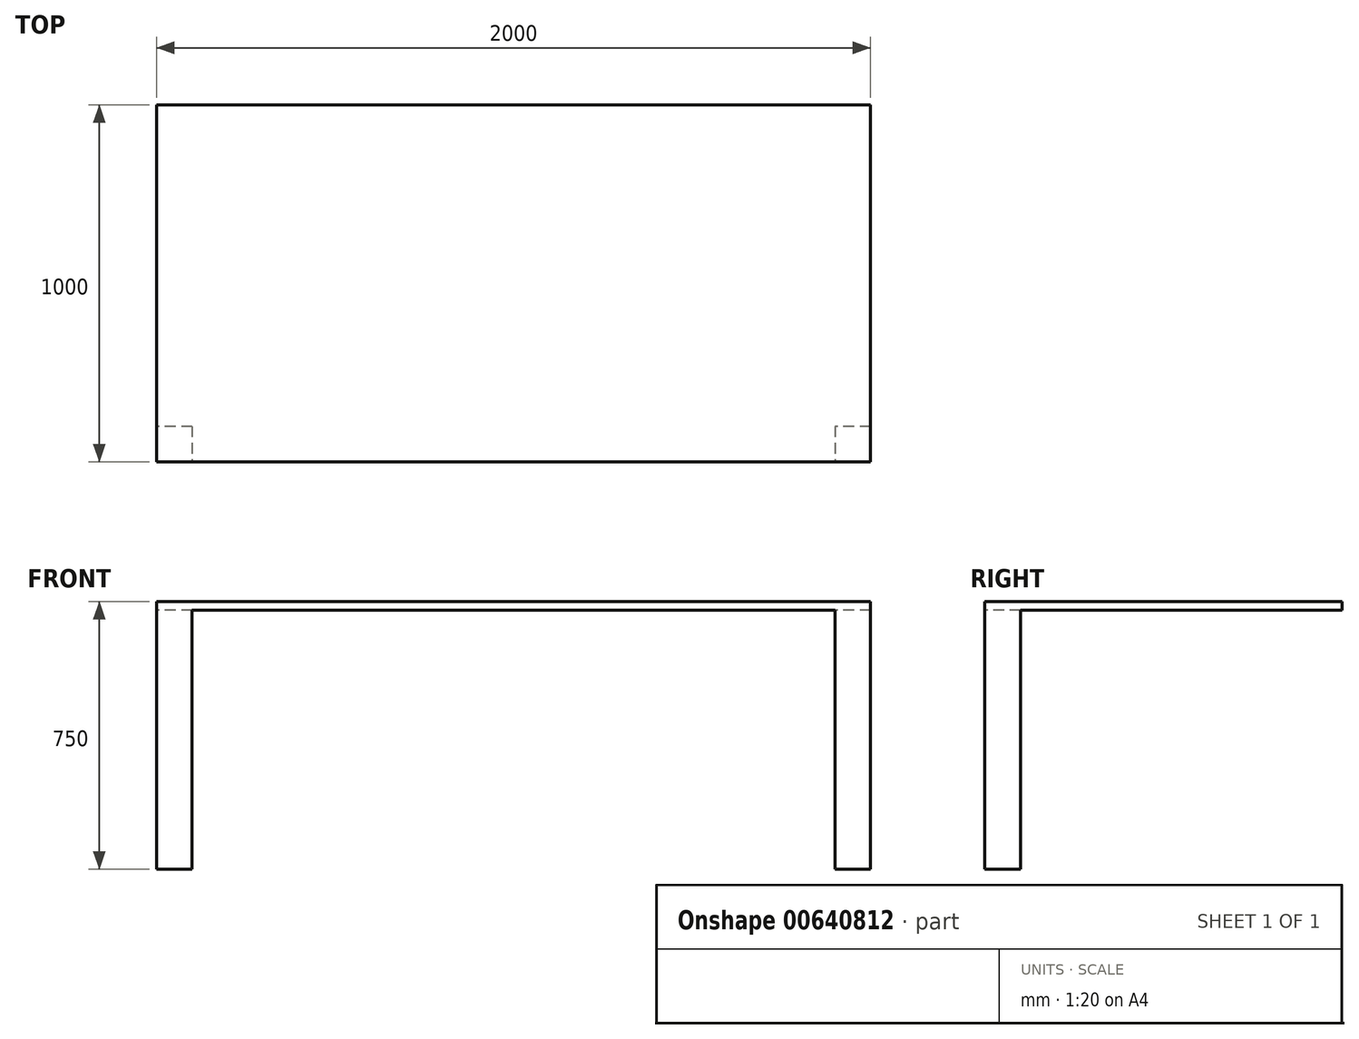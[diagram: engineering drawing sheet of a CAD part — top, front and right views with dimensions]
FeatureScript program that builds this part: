
annotation { "Feature Type Name" : "Feature", "Feature Type Description" : "" }
export const myFeature = defineFeature(function(context is Context, id is Id, definition is map)
    precondition{}
    {
        {
            var Q0;
            Q0=qCreatedBy(makeId("Top.planeOp"),FACE);
            var sketch = newSketch(context, id + "F0", { "sketchPlane" : qUnion([Q0])});
            skLineSegment(sketch, "E0.bottom", {"start": v(1000, -500) * mm, "end": v(-1000, -500) * mm});
            skLineSegment(sketch, "E0.top", {"start": v(1000, 500) * mm, "end": v(-1000, 500) * mm});
            skLineSegment(sketch, "E0.left", {"start": v(1000, -500) * mm, "end": v(1000, 500) * mm});
            skLineSegment(sketch, "E0.right", {"start": v(-1000, -500) * mm, "end": v(-1000, 500) * mm});
            skPoint(sketch, "E1.middle", {"position": v(0, 0) * mm});
            skSolve(sketch);
        }
        {
            var Q0;
            Q0 = qSketchRegion(id + "F0", true);
            extrude(context, id + "F1", {"entities" : qUnion([Q0]), "depth" : 25 * mm, "offsetDistance" : 25 * mm});
        }
        {
            var Q0;
            Q0=makeQuery(id+"F1.opExtrude","CAP_FACE",FACE,{"disambiguationData":[OSD([sQuery(id+"F0.wireOp",EDGE,"E0.bottom"),sQuery(id+"F0.wireOp",EDGE,"E0.top"),sQuery(id+"F0.wireOp",EDGE,"E0.left"),sQuery(id+"F0.wireOp",EDGE,"E0.right")])],"isStart":true});
            var sketch = newSketch(context, id + "F2", { "sketchPlane" : qUnion([Q0])});
            skLineSegment(sketch, "E2.bottom", {"start": v(-900, 400) * mm, "end": v(-1000, 400) * mm});
            skLineSegment(sketch, "E2.top", {"start": v(-900, 500) * mm, "end": v(-1000, 500) * mm});
            skLineSegment(sketch, "E2.left", {"start": v(-900, 400) * mm, "end": v(-900, 500) * mm});
            skLineSegment(sketch, "E2.right", {"start": v(-1000, 400) * mm, "end": v(-1000, 500) * mm});
            skPoint(sketch, "E2.middle", {"position": v(-950, 450) * mm});
            skPoint(sketch, "E3.1.0.0", {"position": v(950, 450) * mm});
            skLineSegment(sketch, "E3.1.0.1", {"start": v(1000, 400) * mm, "end": v(900, 400) * mm});
            skLineSegment(sketch, "E3.1.0.2", {"start": v(900, 400) * mm, "end": v(900, 500) * mm});
            skLineSegment(sketch, "E3.1.0.3", {"start": v(1000, 500) * mm, "end": v(900, 500) * mm});
            skLineSegment(sketch, "E3.1.0.4", {"start": v(1000, 400) * mm, "end": v(1000, 500) * mm});
            skLineSegment(sketch, "E3.direction1", {"start": v(-1000, 400) * mm, "end": v(900, 400) * mm, "construction": true});
            skSolve(sketch);
        }
        {
            var Q0;
            Q0 = qSketchRegion(id + "F2", true);
            extrude(context, id + "F3", {"entities" : qUnion([Q0]), "operationType" : NewBodyOperationType.ADD, "depth" : 725 * mm, "offsetDistance" : 25 * mm});
        }
    });
